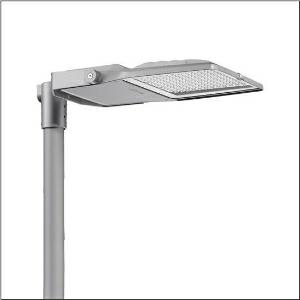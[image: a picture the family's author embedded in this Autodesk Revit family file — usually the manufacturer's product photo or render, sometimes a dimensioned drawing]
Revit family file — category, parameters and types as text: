
# Revit family: floodlight_fl_21_midi___pl64_5xa7786f2e3a_6eef
name_source: partatom
category: Lighting Fixtures
units: mm (PartAtom-declared; Revit-internal decimal feet)

## family parameters
Cut with Voids When Loaded = No
Host = Face
Light Source = No
Part Type = Normal
Room Calculation Point = No
Round Connector Dimension = Use Diameter
Shared = No

## types (1)
- --- (1 x LED, 34530 lm, 271.6 W, 3000K)
    Apparent Load = 272 VA
    CIE Flux Codes = 28 80 98 100 100
    Color Rendering = 70
    Color Temperature = 3000K
    Default Elevation = 1800 mm
    Description = Floodlight FL 21 midi, floodlight, primary light control with lens, of PMMA, primary optical cover: protective disc, of toughened safety glass, transparent, light distribution: PL64, light emission: direct distribution, installation type: surface-mounted, LED, High Power LED, rated luminous flux: 34.530lm, luminous efficacy: 127lm/W, light colour: 730, colour temperature: 3000K, control gear: Smart Interface (Zhaga), control: flexible luminous flux parameterisation, time-dependent luminous flux control, constant luminous flux control, overheat protection, pre-setting: logarithmic dimming characteristic, with terminal, 6-pole, mains connection: 220..240V, AC, 50/60Hz, start of lifetime: 272W, end of service life: 287W, reduction: 123W, luminaire housing, of diecast aluminium, powder-coated, SITECO metallic grey (DB 702S), corrosivity category C5 mid according to DIN EN ISO 12944, suitable for swimming pools, chlorine-resistant, sealing non-destructively replaceable, please order mast flange separately, mast bracket, of steel, galvanised, powder-coated, SITECO metallic grey (DB 702S), Smart Interface below and above, protection rating (complete): IP66, insulation class (complete): insulation class II (safety insulation), certification: CE, ENEC, VDE, protection symbol: D, impact resistance: IK08, permissible operating ambient temperature: -40..+40°C, permissible operating ambient temperature for outdoor applications: -40..+50°C, standard: DIN EN 12944, LABS conformity tested according to VDMA 24364:2018-05, packaging unit: 1 piece

Light Distribution: PL64
    Height = 76 mm
    Lamp = 1 x LED
    Lamp Light Flux = 34530 lm
    Lamp Power = 271.6 W
    Lamp count = 1
    Length = 657 mm
    Luminous efficacy = 127 lm/W
    Manufacturer = Siteco
    ModVariant = No
    Model = 5XA7786F2E3A
    Number of Poles = 1
    OnlyDefault = Yes
    Power Factor = 1
    Product Name = Floodlight FL 21 midi | PL64
    Product group = floodlight | pylon annexe
    ProductGroupID = 6201
    Protection Class = Protection class II
    Protection Degree = IP 66
    RLX_Detail_Level = 1
    RLX_Emergency_Light_Flux = 0 lm
    RLX_Emergency_Type = 0
    RLX_Emergency_Type_DB = No
    RlxData = <blob elided: 153673 chars, md5=2895c6b9>
    Socket = socket
    Standby Power = 0 W
    System Light Flux = 34530 lm
    System Power = 272 W
    Type Comments = factory setting: luminous flux: 100 % | dim-lin: 254 | 620 mA
    Type Image = l_1007123.jpg
    URL = http://relux.com
    VarID = @adj_178933
    Voltage = 0 V
    Weight = 0.00 kg
    Width = 442 mm

## geometry (parser evidence)
native form markers: Blend x4, Sweep x14
no freeform markers — native parametric forms only
